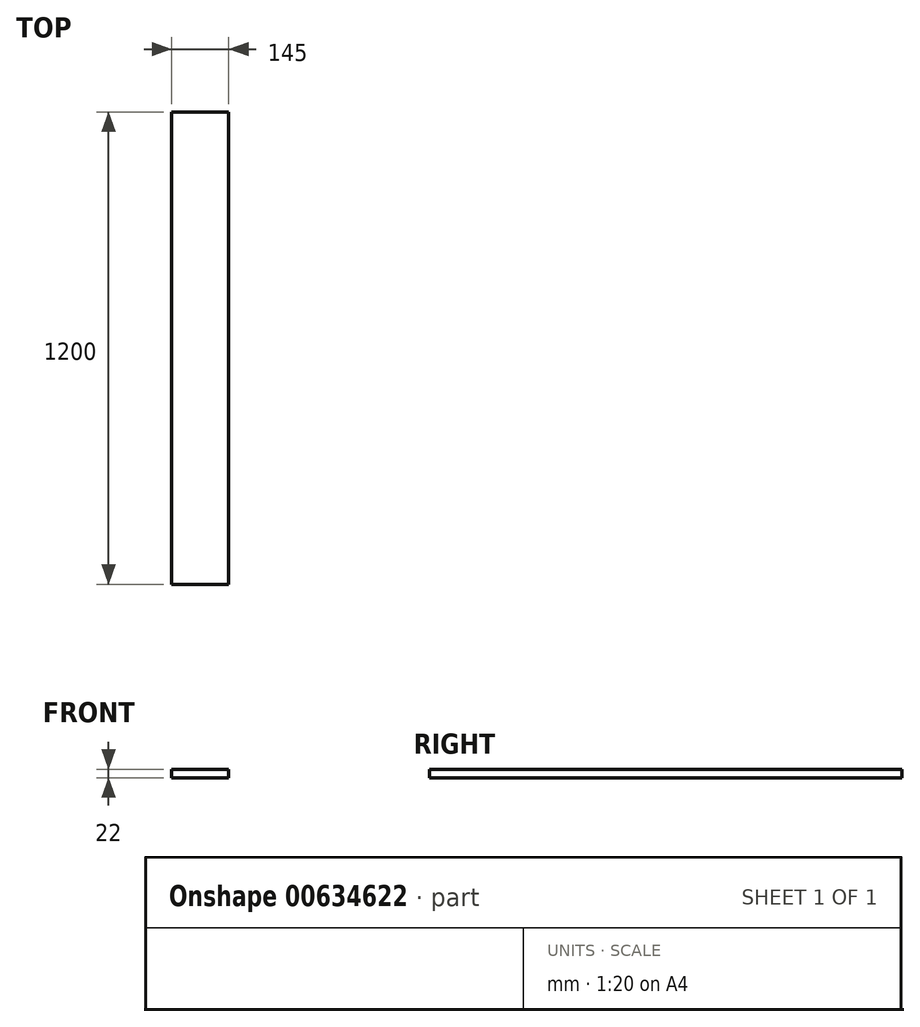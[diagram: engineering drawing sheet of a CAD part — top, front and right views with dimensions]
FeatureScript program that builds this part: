
annotation { "Feature Type Name" : "Feature", "Feature Type Description" : "" }
export const myFeature = defineFeature(function(context is Context, id is Id, definition is map)
    precondition{}
    {
        {
            var Q0;
            Q0=qCreatedBy(makeId("Top.planeOp"),FACE);
            var sketch = newSketch(context, id + "F0", { "sketchPlane" : qUnion([Q0])});
            skLineSegment(sketch, "E0.bottom", {"start": v(0, 0) * mm, "end": v(145, 0) * mm});
            skLineSegment(sketch, "E0.top", {"start": v(0, 1200) * mm, "end": v(145, 1200) * mm});
            skLineSegment(sketch, "E0.left", {"start": v(0, 0) * mm, "end": v(0, 1200) * mm});
            skLineSegment(sketch, "E0.right", {"start": v(145, 0) * mm, "end": v(145, 1200) * mm});
            skSolve(sketch);
        }
        {
            var Q0;
            Q0=qSketchRegion(id+"F0",true);
            extrude(context, id + "F1", {"entities" : qUnion([Q0]), "depth" : 22 * mm, "offsetDistance" : 25 * mm});
        }
    });
